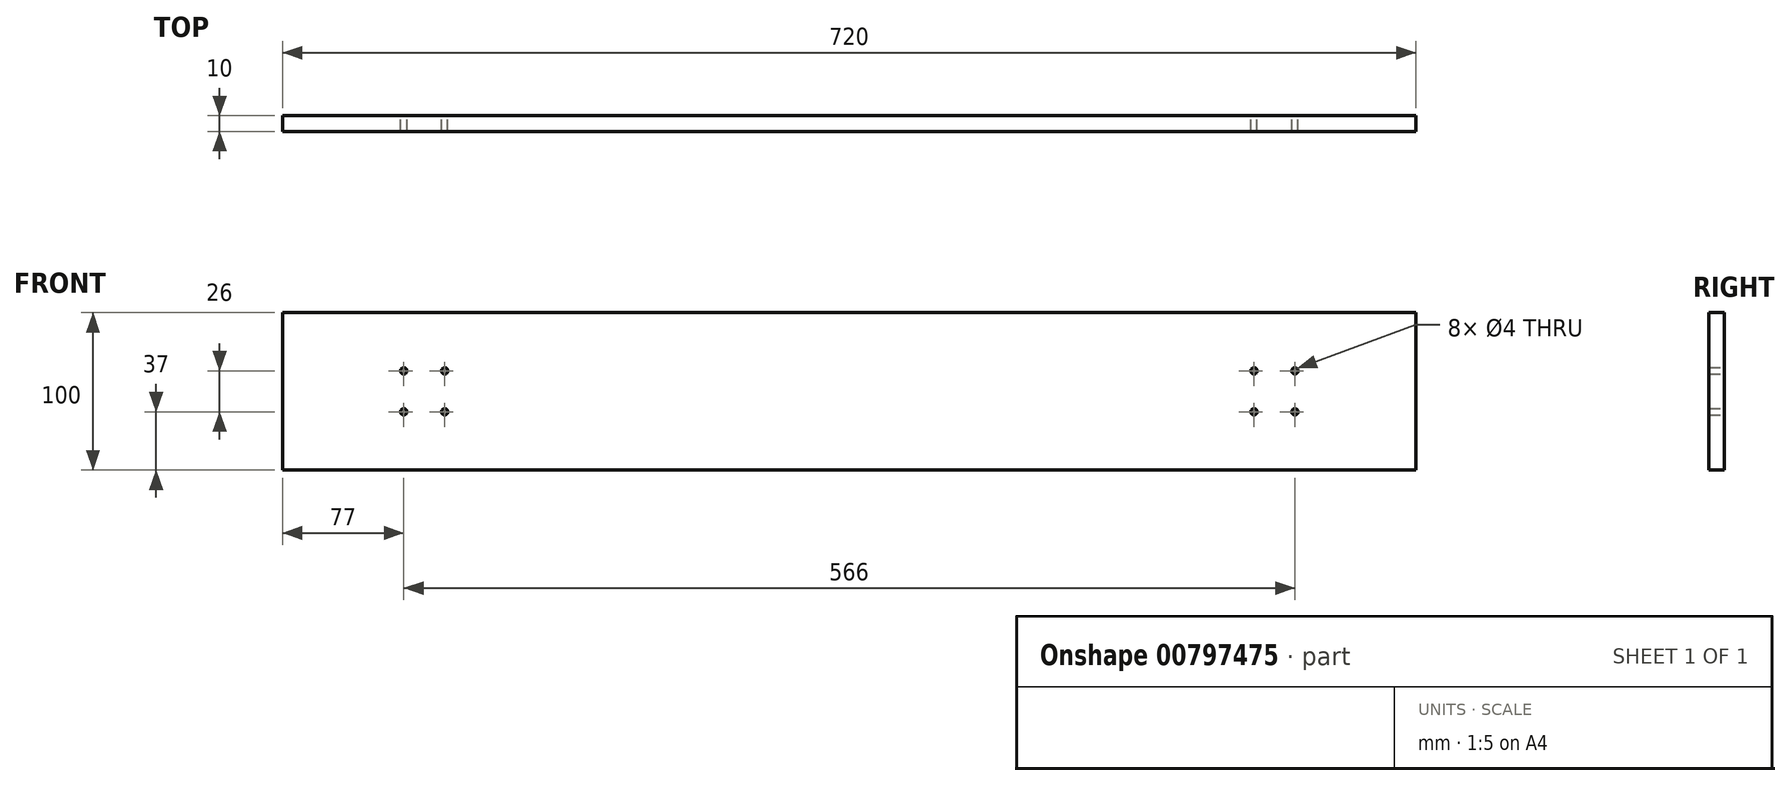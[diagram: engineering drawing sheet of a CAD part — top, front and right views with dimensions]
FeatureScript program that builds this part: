
annotation { "Feature Type Name" : "Feature", "Feature Type Description" : "" }
export const myFeature = defineFeature(function(context is Context, id is Id, definition is map)
    precondition{}
    {
        {
            var Q0;
            Q0=qCreatedBy(makeId("Front.planeOp"),FACE);
            var sketch = newSketch(context, id + "F0", { "sketchPlane" : qUnion([Q0])});
            skLineSegment(sketch, "E0.bottom", {"start": v(360, -50) * mm, "end": v(-360, -50) * mm});
            skLineSegment(sketch, "E0.top", {"start": v(360, 50) * mm, "end": v(-360, 50) * mm});
            skLineSegment(sketch, "E0.left", {"start": v(360, -50) * mm, "end": v(360, 50) * mm});
            skLineSegment(sketch, "E0.right", {"start": v(-360, -50) * mm, "end": v(-360, 50) * mm});
            skPoint(sketch, "E0.middle", {"position": v(0, 0) * mm});
            skLineSegment(sketch, "E1", {"start": v(0, 50) * mm, "end": v(0, -50) * mm, "construction": true});
            skCircle(sketch, "E2", {"center": v(-283, 13) * mm, "radius": 2 * mm});
            skCircle(sketch, "E3", {"center": v(-283, -13) * mm, "radius": 2 * mm});
            skLineSegment(sketch, "E4", {"start": v(-270, 13) * mm, "end": v(-270, -13) * mm, "construction": true});
            skLineSegment(sketch, "E5", {"start": v(-360, 0) * mm, "end": v(-270, 0) * mm, "construction": true});
            skCircle(sketch, "E6.MirrorC", {"center": v(-257, -13) * mm, "radius": 2 * mm});
            skCircle(sketch, "E7.MirrorC", {"center": v(-257, 13) * mm, "radius": 2 * mm});
            skLineSegment(sketch, "E8.MirrorCS", {"start": v(270, 13) * mm, "end": v(270, -13) * mm, "construction": true});
            skCircle(sketch, "E9.MirrorC", {"center": v(283, -13) * mm, "radius": 2 * mm});
            skCircle(sketch, "E10.MirrorC", {"center": v(283, 13) * mm, "radius": 2 * mm});
            skLineSegment(sketch, "E11.MirrorCS", {"start": v(360, 0) * mm, "end": v(270, 0) * mm, "construction": true});
            skCircle(sketch, "E12.MirrorC", {"center": v(257, -13) * mm, "radius": 2 * mm});
            skCircle(sketch, "E13.MirrorC", {"center": v(257, 13) * mm, "radius": 2 * mm});
            skSolve(sketch);
        }
        {
            var Q0;
            Q0 = qSketchRegion(id + "F0", true);
            extrude(context, id + "F1", {"entities" : qUnion([Q0]), "depth" : 10 * mm, "offsetDistance" : 25 * mm});
        }
    });
